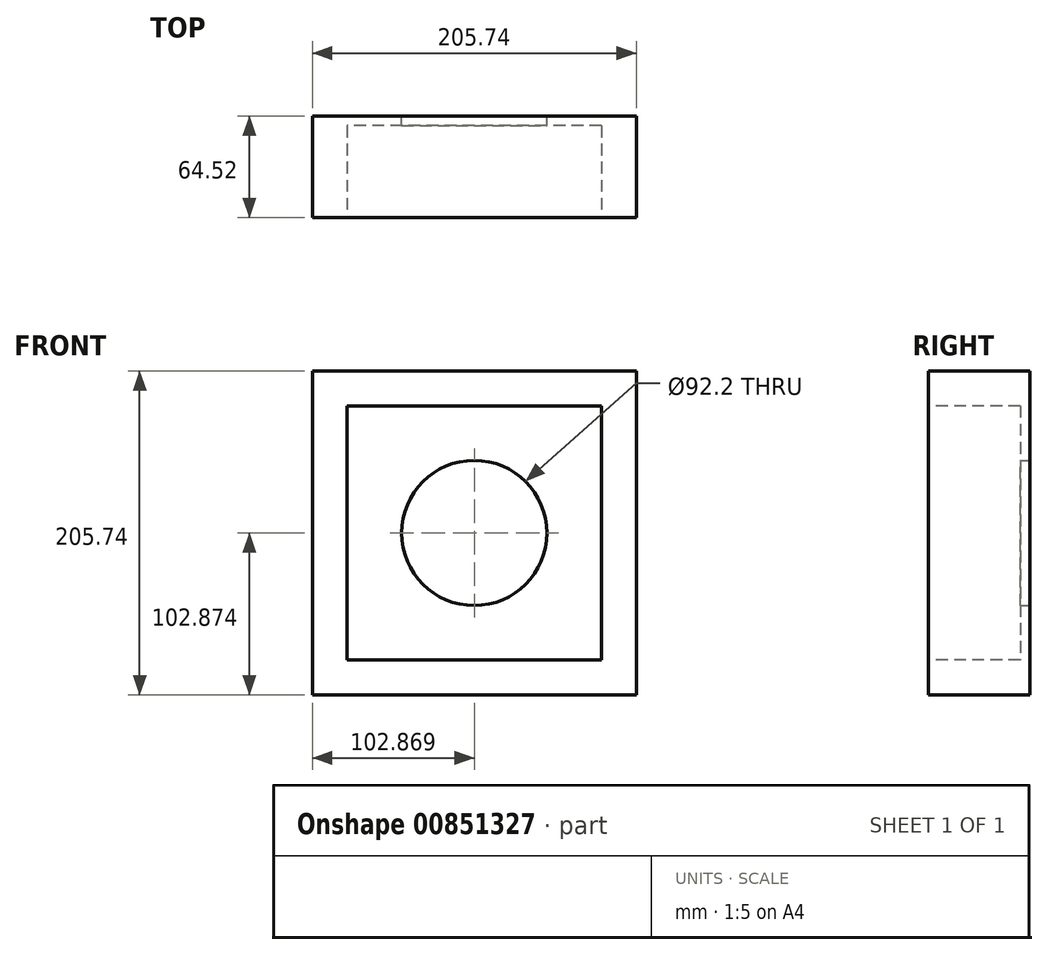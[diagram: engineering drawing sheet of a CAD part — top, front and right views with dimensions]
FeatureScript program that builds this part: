
annotation { "Feature Type Name" : "Feature", "Feature Type Description" : "" }
export const myFeature = defineFeature(function(context is Context, id is Id, definition is map)
    precondition{}
    {
        {
            var Q0;
            Q0=qCreatedBy(makeId("Front.planeOp"),FACE);
            var sketch = newSketch(context, id + "F0", { "sketchPlane" : qUnion([Q0])});
            skLineSegment(sketch, "E0.bottom", {"start": v(-162.27, 100.78) * mm, "end": v(43.47, 100.78) * mm});
            skLineSegment(sketch, "E0.top", {"start": v(-162.27, -104.96) * mm, "end": v(43.47, -104.96) * mm});
            skLineSegment(sketch, "E0.left", {"start": v(-162.27, 100.78) * mm, "end": v(-162.27, -104.96) * mm});
            skLineSegment(sketch, "E0.right", {"start": v(43.47, 100.78) * mm, "end": v(43.47, -104.96) * mm});
            skCircle(sketch, "E1", {"center": v(-59.4, -2.09) * mm, "radius": 46.1 * mm});
            skPoint(sketch, "E1.perimeterSnap0", {"position": v(-59.4, -2.09) * mm});
            skSolve(sketch);
        }
        {
            var Q0;
            Q0 = qSketchRegion(id + "F0", true);
            extrude(context, id + "F1", {"entities" : qUnion([Q0]), "depth" : 64.52 * mm, "offsetDistance" : 25.4 * mm});
        }
        {
            var Q0;
            Q0=makeQuery(id+"F1.opExtrude","CAP_FACE",FACE,{"disambiguationData":[OSD([sQuery(id+"F0.wireOp",EDGE,"E0.bottom"),sQuery(id+"F0.wireOp",EDGE,"E0.top"),sQuery(id+"F0.wireOp",EDGE,"E0.left"),sQuery(id+"F0.wireOp",EDGE,"E0.right"),sQuery(id+"F0.wireOp",EDGE,"E1")])],"isStart":false});
            var sketch = newSketch(context, id + "F2", { "sketchPlane" : qUnion([Q0])});
            skLineSegment(sketch, "E2.bottom", {"start": v(21.37, 78.69) * mm, "end": v(-140.17, 78.69) * mm});
            skLineSegment(sketch, "E2.top", {"start": v(21.37, -82.86) * mm, "end": v(-140.17, -82.86) * mm});
            skLineSegment(sketch, "E2.left", {"start": v(21.37, 78.69) * mm, "end": v(21.37, -82.86) * mm});
            skLineSegment(sketch, "E2.right", {"start": v(-140.17, 78.69) * mm, "end": v(-140.17, -82.86) * mm});
            skPoint(sketch, "E2.middle", {"position": v(-59.4, -2.09) * mm});
            skSolve(sketch);
        }
        {
            var Q0;
            Q0=makeQuery(id+"F2.imprint","IMPRINT",FACE,{"disambiguationData":[TD([[makeQuery(id+"F2.imprint","IMPRINT",EDGE,{"derivedFrom":sQuery(id+"F2.wireOp",EDGE,"E2.bottom")}),1.0]])]});
            var Q1;
            Q1=sQuery(id+"F2.wireOp",EDGE,"E2.bottom");
            var Q2;
            Q2=sQuery(id+"F2.wireOp",EDGE,"E2.left");
            var Q3;
            Q3=sQuery(id+"F2.wireOp",EDGE,"E2.top");
            var Q4;
            Q4=sQuery(id+"F2.wireOp",EDGE,"E2.right");
            extrude(context, id + "F3", {"entities" : qUnion([Q0]), "operationType" : NewBodyOperationType.REMOVE, "surfaceEntities" : qUnion([Q1, Q2, Q3, Q4]), "oppositeDirection" : true, "depth" : 58.42 * mm, "offsetDistance" : 25.4 * mm});
        }
    });
